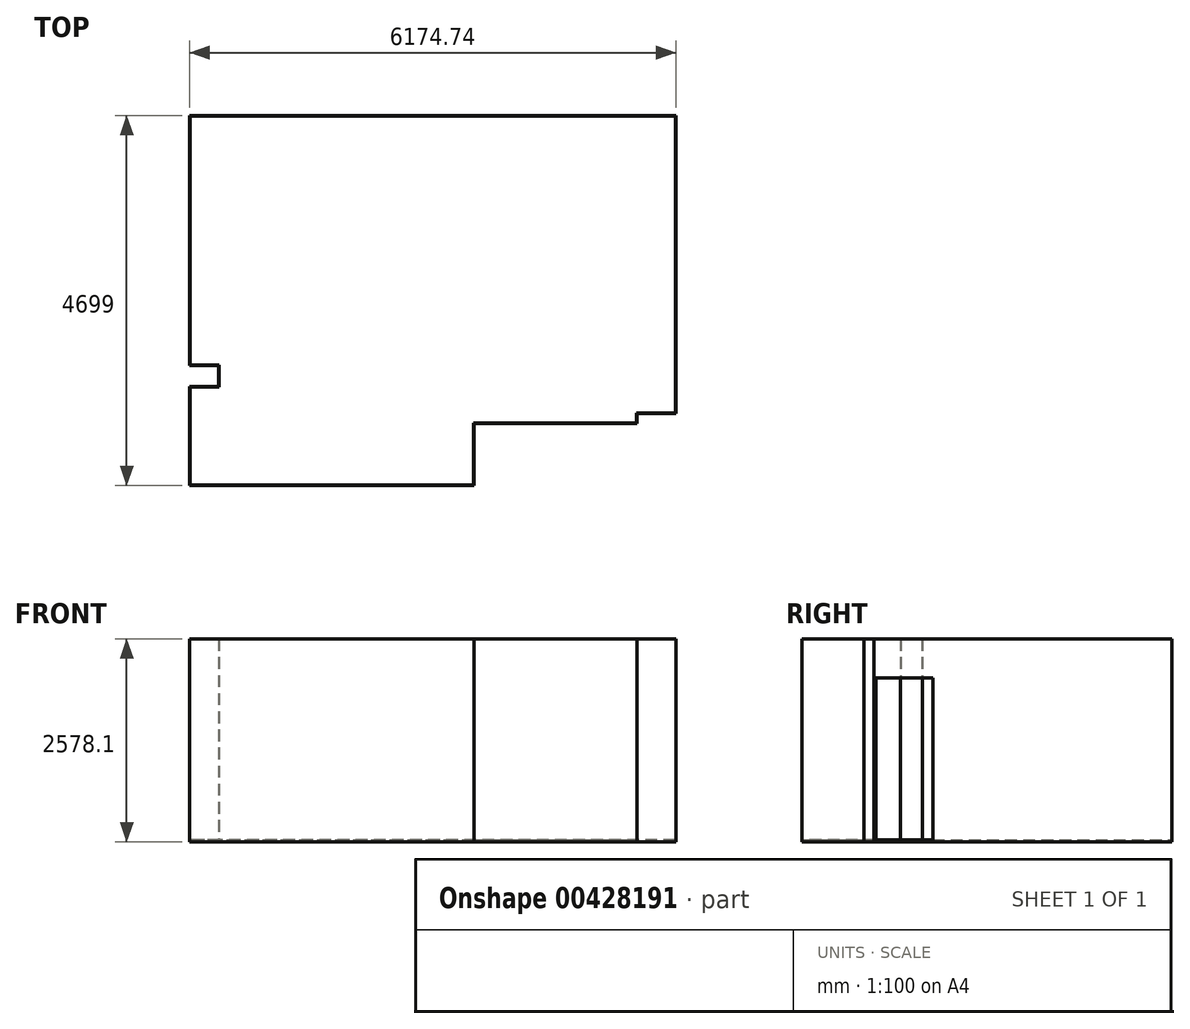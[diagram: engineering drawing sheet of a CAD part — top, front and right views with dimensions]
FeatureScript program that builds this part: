
annotation { "Feature Type Name" : "Feature", "Feature Type Description" : "" }
export const myFeature = defineFeature(function(context is Context, id is Id, definition is map)
    precondition{}
    {
        {
            var Q0;
            Q0=qCreatedBy(makeId("Top.planeOp"),FACE);
            var sketch = newSketch(context, id + "F0", { "sketchPlane" : qUnion([Q0])});
            skLineSegment(sketch, "E0", {"start": v(0, 0) * mm, "end": v(3596.64, 0) * mm});
            skLineSegment(sketch, "E1", {"start": v(3596.64, 0) * mm, "end": v(3596.64, 787.4) * mm});
            skLineSegment(sketch, "E2", {"start": v(3596.64, 787.4) * mm, "end": v(5666.74, 787.4) * mm});
            skLineSegment(sketch, "E3", {"start": v(6162.04, 914.4) * mm, "end": v(6162.04, 4686.3) * mm});
            skLineSegment(sketch, "E4", {"start": v(6162.04, 4686.3) * mm, "end": v(0, 4686.3) * mm});
            skLineSegment(sketch, "E5", {"start": v(0, 4686.3) * mm, "end": v(0, 1524) * mm});
            skLineSegment(sketch, "E6", {"start": v(0, 1524) * mm, "end": v(368.3, 1524) * mm});
            skLineSegment(sketch, "E7", {"start": v(368.3, 1524) * mm, "end": v(368.3, 1244.6) * mm});
            skLineSegment(sketch, "E8", {"start": v(368.3, 1244.6) * mm, "end": v(0, 1244.6) * mm});
            skLineSegment(sketch, "E9", {"start": v(0, 1244.6) * mm, "end": v(0, 0) * mm});
            skLineSegment(sketch, "E10", {"start": v(6162.04, 914.4) * mm, "end": v(5666.74, 914.4) * mm});
            skLineSegment(sketch, "E11", {"start": v(5666.74, 914.4) * mm, "end": v(5666.74, 787.4) * mm});
            skLineSegment(sketch, "E12.0", {"start": v(6168.4, 4692.65) * mm, "end": v(-6.35, 4692.65) * mm});
            skLineSegment(sketch, "E12.1", {"start": v(-6.35, 1250.95) * mm, "end": v(-6.35, -6.35) * mm});
            skLineSegment(sketch, "E12.2", {"start": v(361.95, 1250.95) * mm, "end": v(-6.35, 1250.95) * mm});
            skLineSegment(sketch, "E12.3", {"start": v(361.95, 1517.65) * mm, "end": v(361.95, 1250.95) * mm});
            skLineSegment(sketch, "E12.4", {"start": v(-6.35, 1517.65) * mm, "end": v(361.95, 1517.65) * mm});
            skLineSegment(sketch, "E12.5", {"start": v(-6.35, -6.35) * mm, "end": v(3603, -6.35) * mm});
            skLineSegment(sketch, "E12.6", {"start": v(-6.35, 4692.65) * mm, "end": v(-6.35, 1517.65) * mm});
            skLineSegment(sketch, "E12.7", {"start": v(3603, -6.35) * mm, "end": v(3603, 781.05) * mm});
            skLineSegment(sketch, "E12.8", {"start": v(3603, 781.05) * mm, "end": v(5673.1, 781.05) * mm});
            skLineSegment(sketch, "E12.9", {"start": v(5673.1, 908.05) * mm, "end": v(5673.1, 781.05) * mm});
            skLineSegment(sketch, "E12.10", {"start": v(6168.4, 908.05) * mm, "end": v(5673.1, 908.05) * mm});
            skLineSegment(sketch, "E12.11", {"start": v(6168.4, 908.05) * mm, "end": v(6168.4, 4692.65) * mm});
            skSolve(sketch);
        }
        {
            var Q0;
            Q0=makeQuery(id+"F0.imprint","IMPRINT",FACE,{"disambiguationData":[TD([[makeQuery(id+"F0.imprint","IMPRINT",EDGE,{"derivedFrom":sQuery(id+"F0.wireOp",EDGE,"E0")}),-1.0]])]});
            extrude(context, id + "F1", {"entities" : qUnion([Q0]), "depth" : 2552.7 * mm});
        }
        {
            var Q0;
            Q0=makeQuery(id+"F1.opExtrude","CAP_FACE",FACE,{"disambiguationData":[OSD([sQuery(id+"F0.wireOp",EDGE,"E0"),sQuery(id+"F0.wireOp",EDGE,"E1"),sQuery(id+"F0.wireOp",EDGE,"E2"),sQuery(id+"F0.wireOp",EDGE,"E3"),sQuery(id+"F0.wireOp",EDGE,"E4"),sQuery(id+"F0.wireOp",EDGE,"E5"),sQuery(id+"F0.wireOp",EDGE,"E6"),sQuery(id+"F0.wireOp",EDGE,"E7"),sQuery(id+"F0.wireOp",EDGE,"E8"),sQuery(id+"F0.wireOp",EDGE,"E9"),sQuery(id+"F0.wireOp",EDGE,"E10"),sQuery(id+"F0.wireOp",EDGE,"E11"),sQuery(id+"F0.wireOp",EDGE,"E12.0"),sQuery(id+"F0.wireOp",EDGE,"E12.1"),sQuery(id+"F0.wireOp",EDGE,"E12.2"),sQuery(id+"F0.wireOp",EDGE,"E12.3"),sQuery(id+"F0.wireOp",EDGE,"E12.4"),sQuery(id+"F0.wireOp",EDGE,"E12.5"),sQuery(id+"F0.wireOp",EDGE,"E12.6"),sQuery(id+"F0.wireOp",EDGE,"E12.7"),sQuery(id+"F0.wireOp",EDGE,"E12.8"),sQuery(id+"F0.wireOp",EDGE,"E12.9"),sQuery(id+"F0.wireOp",EDGE,"E12.10"),sQuery(id+"F0.wireOp",EDGE,"E12.11")])],"isStart":true});
            var sketch = newSketch(context, id + "F2", { "sketchPlane" : qUnion([Q0])});
            skLineSegment(sketch, "E13.0", {"start": v(6168.4, -4692.65) * mm, "end": v(-6.35, -4692.65) * mm});
            skLineSegment(sketch, "E14.0", {"start": v(6168.4, -908.05) * mm, "end": v(6168.4, -4692.65) * mm});
            skLineSegment(sketch, "E15.0", {"start": v(6168.4, -908.05) * mm, "end": v(5673.1, -908.05) * mm});
            skLineSegment(sketch, "E15.1", {"start": v(5673.1, -908.05) * mm, "end": v(5673.1, -781.05) * mm});
            skLineSegment(sketch, "E15.2", {"start": v(3603, -781.05) * mm, "end": v(5673.1, -781.05) * mm});
            skLineSegment(sketch, "E16.0", {"start": v(3603, 6.35) * mm, "end": v(3603, -781.05) * mm});
            skLineSegment(sketch, "E16.1", {"start": v(-6.35, 6.35) * mm, "end": v(3603, 6.35) * mm});
            skLineSegment(sketch, "E16.2", {"start": v(-6.35, -1250.95) * mm, "end": v(-6.35, 6.35) * mm});
            skLineSegment(sketch, "E16.3", {"start": v(361.95, -1250.95) * mm, "end": v(-6.35, -1250.95) * mm});
            skLineSegment(sketch, "E16.4", {"start": v(361.95, -1517.65) * mm, "end": v(361.95, -1250.95) * mm});
            skLineSegment(sketch, "E16.5", {"start": v(-6.35, -1517.65) * mm, "end": v(361.95, -1517.65) * mm});
            skLineSegment(sketch, "E16.6", {"start": v(-6.35, -4692.65) * mm, "end": v(-6.35, -1517.65) * mm});
            skSolve(sketch);
        }
        {
            var Q0;
            Q0 = qSketchRegion(id + "F2", true);
            extrude(context, id + "F3", {"entities" : qUnion([Q0]), "operationType" : NewBodyOperationType.ADD, "depth" : 25.4 * mm});
        }
        {
            var Q0;
            Q0=makeQuery(id+"F3.boolean.opBoolean","MERGE",FACE,{"derivedFrom":[makeQuery(id+"F1.opExtrude","SWEPT_FACE",FACE,{"disambiguationData":[OSD([sQuery(id+"F0.wireOp",EDGE,"E12.11")])]}),makeQuery(id+"F3.opExtrude","SWEPT_FACE",FACE,{"disambiguationData":[OSD([sQuery(id+"F2.wireOp",EDGE,"E14.0")])]})]});
            var sketch = newSketch(context, id + "F4", { "sketchPlane" : qUnion([Q0])});
            skLineSegment(sketch, "E17.bottom", {"start": v(933.45, 0) * mm, "end": v(1657.35, 0) * mm});
            skLineSegment(sketch, "E17.top", {"start": v(933.45, 2060.57) * mm, "end": v(1657.35, 2060.57) * mm});
            skLineSegment(sketch, "E17.left", {"start": v(933.45, 0) * mm, "end": v(933.45, 2060.57) * mm});
            skLineSegment(sketch, "E17.right", {"start": v(1657.35, 0) * mm, "end": v(1657.35, 2060.57) * mm});
            skSolve(sketch);
        }
        {
            var Q0;
            Q0=makeQuery(id+"F4.imprint","IMPRINT",FACE,{"disambiguationData":[TD([[makeQuery(id+"F4.imprint","IMPRINT",EDGE,{"derivedFrom":sQuery(id+"F4.wireOp",EDGE,"E17.bottom")}),1.0]])]});
            extrude(context, id + "F5", {"entities" : qUnion([Q0]), "operationType" : NewBodyOperationType.REMOVE, "endBound" : BoundingType.UP_TO_NEXT, "oppositeDirection" : true, "depth" : 25.4 * mm});
        }
    });
